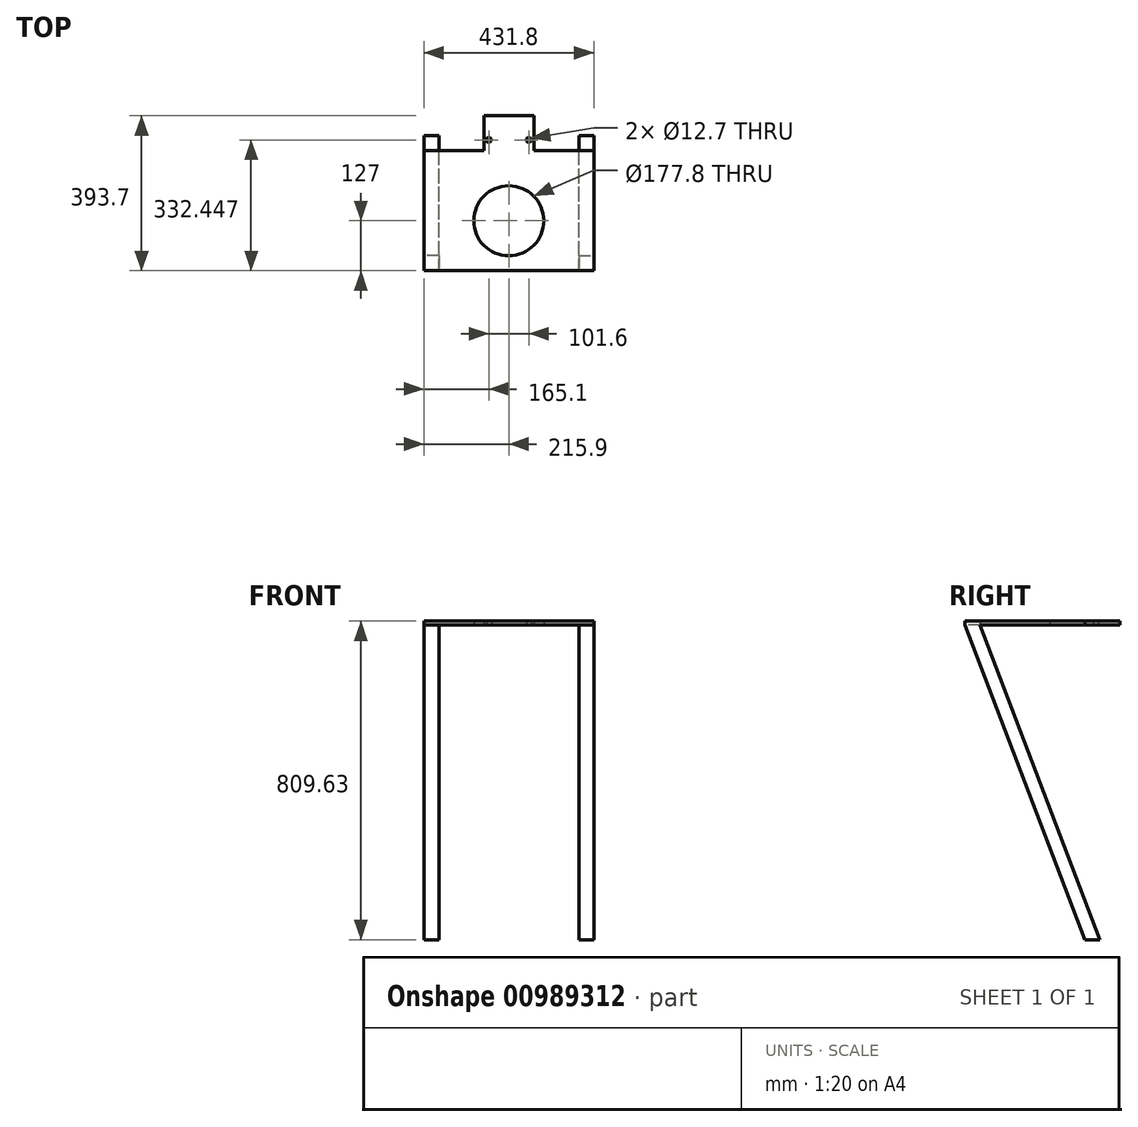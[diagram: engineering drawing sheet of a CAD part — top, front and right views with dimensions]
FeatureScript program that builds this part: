
annotation { "Feature Type Name" : "Feature", "Feature Type Description" : "" }
export const myFeature = defineFeature(function(context is Context, id is Id, definition is map)
    precondition{}
    {
        {
            var Q0;
            Q0=qCreatedBy(makeId("Top.planeOp"),FACE);
            var sketch = newSketch(context, id + "F0", { "sketchPlane" : qUnion([Q0])});
            skLineSegment(sketch, "E0.bottom", {"start": v(0, 0) * mm, "end": v(127, 0) * mm});
            skLineSegment(sketch, "E0.top", {"start": v(0, 88.9) * mm, "end": v(127, 88.9) * mm});
            skLineSegment(sketch, "E0.left", {"start": v(0, 0) * mm, "end": v(0, 88.9) * mm});
            skLineSegment(sketch, "E0.right", {"start": v(127, 0) * mm, "end": v(127, 88.9) * mm});
            skLineSegment(sketch, "E1.bottom", {"start": v(-152.4, 0) * mm, "end": v(279.4, 0) * mm});
            skLineSegment(sketch, "E1.top", {"start": v(-152.4, -304.8) * mm, "end": v(279.4, -304.8) * mm});
            skLineSegment(sketch, "E1.left", {"start": v(-152.4, 0) * mm, "end": v(-152.4, -304.8) * mm});
            skLineSegment(sketch, "E1.right", {"start": v(279.4, 0) * mm, "end": v(279.4, -304.8) * mm});
            skCircle(sketch, "E2", {"center": v(12.7, 27.65) * mm, "radius": 6.35 * mm});
            skCircle(sketch, "E3", {"center": v(114.3, 27.65) * mm, "radius": 6.35 * mm});
            skCircle(sketch, "E4", {"center": v(63.5, -177.8) * mm, "radius": 88.9 * mm});
            skSolve(sketch);
        }
        {
            var Q0;
            Q0 = qSketchRegion(id + "F0", true);
            extrude(context, id + "F1", {"entities" : qUnion([Q0]), "depth" : 9.52 * mm, "offsetDistance" : 25.4 * mm});
        }
        {
            var Q0;
            Q0=makeQuery(id+"F1.opExtrude","SWEPT_FACE",FACE,{"disambiguationData":[OSD([sQuery(id+"F0.wireOp",EDGE,"E1.left")])]});
            var sketch = newSketch(context, id + "F2", { "sketchPlane" : qUnion([Q0])});
            skLineSegment(sketch, "E5", {"start": v(304.8, 0) * mm, "end": v(0, -800.1) * mm});
            skLineSegment(sketch, "E6", {"start": v(266.7, 0) * mm, "end": v(-38.02, -799.9) * mm});
            skLineSegment(sketch, "E7", {"start": v(-38.02, -799.9) * mm, "end": v(0, -800.1) * mm});
            skSolve(sketch);
        }
        {
            var Q0;
            {var subQ0=sQuery(id+"F2.wireOp",EDGE,"E5");Q0=makeQuery(id+"F2.imprint","IMPRINT",FACE,{"disambiguationData":[TD([[makeQuery(id+"F2.imprint","IMPRINT",EDGE,{"derivedFrom":subQ0}),-1.0]])]});}
            extrude(context, id + "F3", {"entities" : qUnion([Q0]), "operationType" : NewBodyOperationType.ADD, "oppositeDirection" : true, "depth" : 38.1 * mm, "offsetDistance" : 25.4 * mm});
        }
        {
            var Q0;
            Q0=makeQuery(id+"F1.opExtrude","SWEPT_FACE",FACE,{"disambiguationData":[OSD([sQuery(id+"F0.wireOp",EDGE,"E1.right")])]});
            var sketch = newSketch(context, id + "F4", { "sketchPlane" : qUnion([Q0])});
            skLineSegment(sketch, "E8", {"start": v(-304.8, 0) * mm, "end": v(0, -800.1) * mm});
            skLineSegment(sketch, "E9", {"start": v(-266.7, 0) * mm, "end": v(38.02, -799.9) * mm});
            skLineSegment(sketch, "E10", {"start": v(-1.08, -800.05) * mm, "end": v(38.02, -799.9) * mm});
            skSolve(sketch);
        }
        {
            var Q0;
            {var subQ6=sQuery(id+"F4.wireOp",EDGE,"E9");Q0=makeQuery(id+"F4.imprint","IMPRINT",FACE,{"disambiguationData":[TD([[makeQuery(id+"F4.imprint","IMPRINT",EDGE,{"derivedFrom":subQ6}),-1.0]])]});}
            extrude(context, id + "F5", {"entities" : qUnion([Q0]), "operationType" : NewBodyOperationType.ADD, "oppositeDirection" : true, "depth" : 38.1 * mm, "offsetDistance" : 25.4 * mm});
        }
    });
